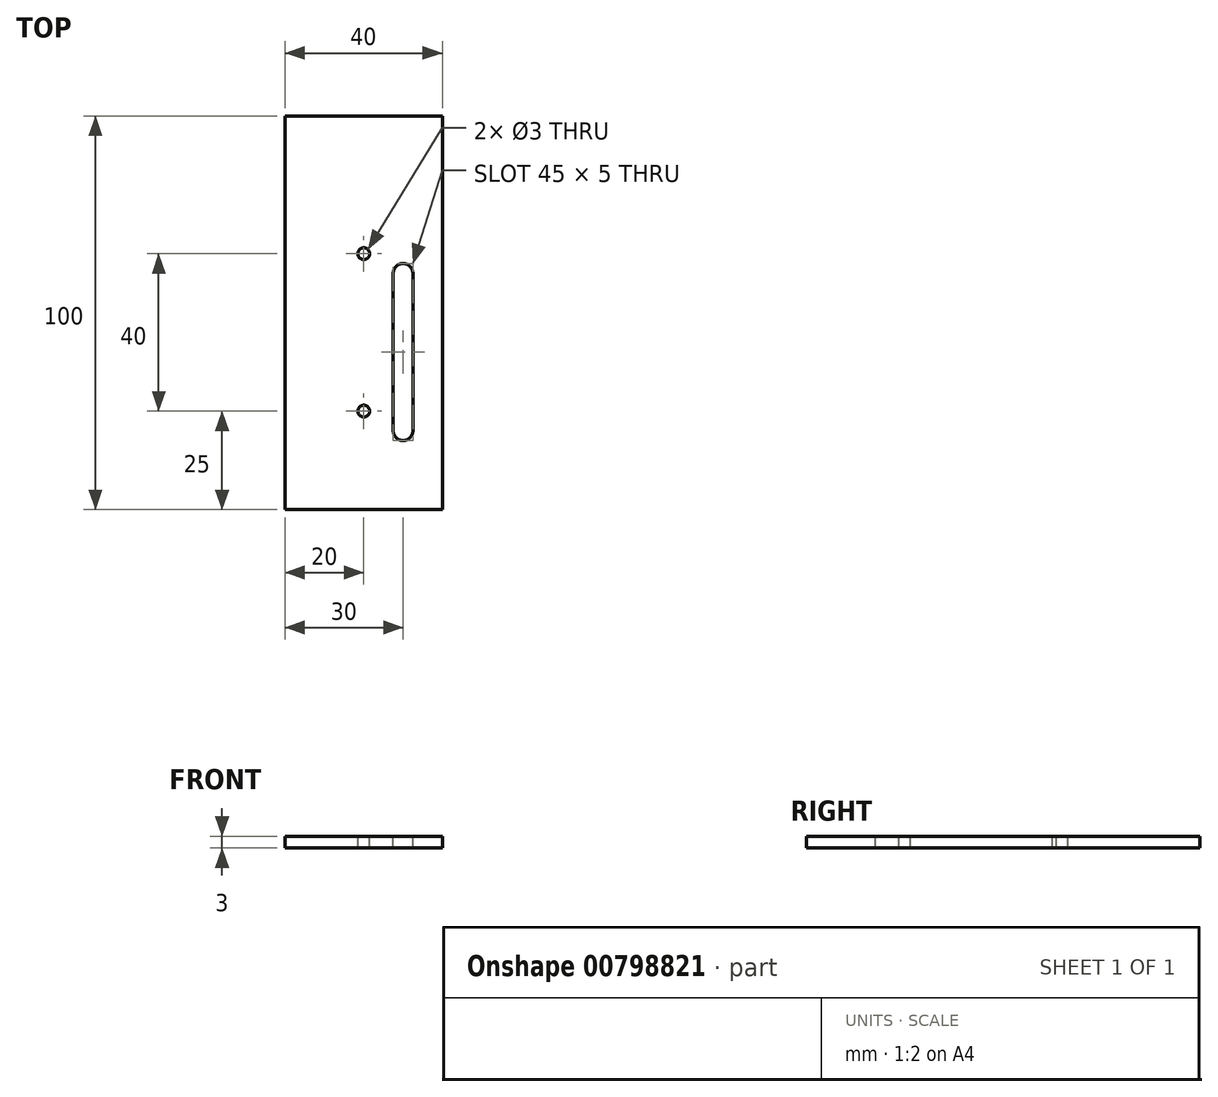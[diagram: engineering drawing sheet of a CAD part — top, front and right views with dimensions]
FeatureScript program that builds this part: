
annotation { "Feature Type Name" : "Feature", "Feature Type Description" : "" }
export const myFeature = defineFeature(function(context is Context, id is Id, definition is map)
    precondition{}
    {
        {
            var Q0;
            Q0=qCreatedBy(makeId("Top.planeOp"),FACE);
            var sketch = newSketch(context, id + "F0", { "sketchPlane" : qUnion([Q0])});
            skLineSegment(sketch, "E0.bottom", {"start": v(0, 0) * mm, "end": v(5.77, 0) * mm});
            skLineSegment(sketch, "E0.top", {"start": v(0, 0) * mm, "end": v(5.77, 0) * mm});
            skLineSegment(sketch, "E0.left", {"start": v(0, 0) * mm, "end": v(0, 0) * mm});
            skLineSegment(sketch, "E0.right", {"start": v(5.77, 0) * mm, "end": v(5.77, 0) * mm});
            skLineSegment(sketch, "E1.bottom", {"start": v(0, 0) * mm, "end": v(40, 0) * mm});
            skLineSegment(sketch, "E1.top", {"start": v(0, 100) * mm, "end": v(40, 100) * mm});
            skLineSegment(sketch, "E1.left", {"start": v(0, 0) * mm, "end": v(0, 100) * mm});
            skLineSegment(sketch, "E1.right", {"start": v(40, 0) * mm, "end": v(40, 100) * mm});
            skSolve(sketch);
        }
        {
            var Q0;
            Q0=makeQuery(id+"F0.imprint","IMPRINT",FACE,{"disambiguationData":[TD([[makeQuery(id+"F0.imprint","IMPRINT",EDGE,{"derivedFrom":sQuery(id+"F0.wireOp",EDGE,"E1.top")}),-1.0]])]});
            extrude(context, id + "F1", {"entities" : qUnion([Q0]), "depth" : 3 * mm, "offsetDistance" : 25 * mm});
        }
        {
            var Q0;
            Q0=makeQuery(id+"F1.opExtrude","CAP_FACE",FACE,{"disambiguationData":[OSD([sQuery(id+"F0.wireOp",EDGE,"E1.bottom"),sQuery(id+"F0.wireOp",EDGE,"E1.top"),sQuery(id+"F0.wireOp",EDGE,"E1.left"),sQuery(id+"F0.wireOp",EDGE,"E1.right")])],"isStart":false});
            var sketch = newSketch(context, id + "F2", { "sketchPlane" : qUnion([Q0])});
            skLineSegment(sketch, "E2", {"start": v(20, 65) * mm, "end": v(20, 25) * mm});
            skSolve(sketch);
        }
        {
            var Q0;
            Q0=sQuery(id+"F2.wireOp",VERTEX,"E2.start");
            var Q1;
            Q1=sQuery(id+"F2.wireOp",VERTEX,"E2.end");
            var Q2;
            Q2=makeQuery(id+"F1.opExtrude","SWEPT_BODY",BODY,{"disambiguationData":[OSD([sQuery(id+"F0.wireOp",EDGE,"E1.bottom"),sQuery(id+"F0.wireOp",EDGE,"E1.top"),sQuery(id+"F0.wireOp",EDGE,"E1.left"),sQuery(id+"F0.wireOp",EDGE,"E1.right")])]});
            hole(context, id + "F3", {"style" : HoleStyle.SIMPLE, "endStyle" : HoleEndStyle.THROUGH, "holeDiameter" : 3 * mm, "majorDiameter" : 5 * mm, "isTappedThrough" : true, "tappedDepth" : 12 * mm, "tapClearance" : 3, "locations" : qUnion([Q0, Q1]), "scope" : qUnion([Q2])});
        }
        {
            var Q0;
            Q0=makeQuery(id+"F1.opExtrude","CAP_FACE",FACE,{"disambiguationData":[OSD([sQuery(id+"F0.wireOp",EDGE,"E1.bottom"),sQuery(id+"F0.wireOp",EDGE,"E1.top"),sQuery(id+"F0.wireOp",EDGE,"E1.left"),sQuery(id+"F0.wireOp",EDGE,"E1.right")])],"isStart":false});
            var sketch = newSketch(context, id + "F4", { "sketchPlane" : qUnion([Q0])});
            skLineSegment(sketch, "E3", {"start": v(30, 20) * mm, "end": v(30, 60) * mm});
            skLineSegment(sketch, "E4", {"start": v(30, 60) * mm, "end": v(30, 20) * mm});
            skSolve(sketch);
        }
        {
            var Q0;
            Q0=makeQuery(id+"F4.imprint","IMPRINT",FACE,{"disambiguationData":[TD([[makeQuery(id+"F4.imprint","IMPRINT",EDGE,{"derivedFrom":makeQuery(id+"F1.opExtrude","CAP_EDGE",EDGE,{"disambiguationData":[OSD([sQuery(id+"F0.wireOp",EDGE,"E1.bottom")])],"isStart":false})}),1.0]])]});
            var sketch = newSketch(context, id + "F5", { "sketchPlane" : qUnion([Q0])});
            skLineSegment(sketch, "E5.JUB.JUB", {"start": v(30, 20) * mm, "end": v(30, 60) * mm, "construction": true});
            skArc(sketch, "E5.0.startCap", {"start": v(32.5, 20) * mm, "mid": v(30, 17.5) * mm, "end": v(27.5, 20) * mm});
            skArc(sketch, "E5.0.endCap", {"start": v(27.5, 60) * mm, "mid": v(30, 62.5) * mm, "end": v(32.5, 60) * mm});
            skLineSegment(sketch, "E5.0.left", {"start": v(27.5, 20) * mm, "end": v(27.5, 60) * mm});
            skLineSegment(sketch, "E5.0.right", {"start": v(32.5, 20) * mm, "end": v(32.5, 60) * mm});
            skSolve(sketch);
        }
        {
            var Q0;
            Q0 = qSketchRegion(id + "F5", true);
            extrude(context, id + "F6", {"entities" : qUnion([Q0]), "operationType" : NewBodyOperationType.REMOVE, "oppositeDirection" : true, "depth" : 25 * mm, "offsetDistance" : 25 * mm});
        }
    });
